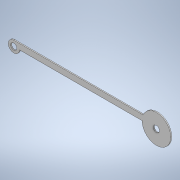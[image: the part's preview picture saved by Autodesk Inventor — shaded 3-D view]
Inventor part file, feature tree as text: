
AUTODESK INVENTOR PART (.ipt)
format: ipt  version: 2022 (Build 260153000, 153)  size: 107,520 bytes
history: native  units: in
note: dims shown in document units (in); Inventor stores cm internally (conversion verified against a paired STEP export)
features: other x1, extrude x1, sketch x1
ambient origin geometry x8: Origin, YZ Plane, XZ Plane, XY Plane, X Axis, Y Axis, Z Axis, Center Point
bodies: Body1 (feature_tree)
feature tree (3):
  other  "Sólido1"
  extrude  "Extrusión1"  Depth=0.0157in
  sketch  "Boceto1"  dims[d9=0.176in d10=0.0984in d12=0.452in d15=0.0878in d16=2.25in d17=0.0157in d18=0.0in]
